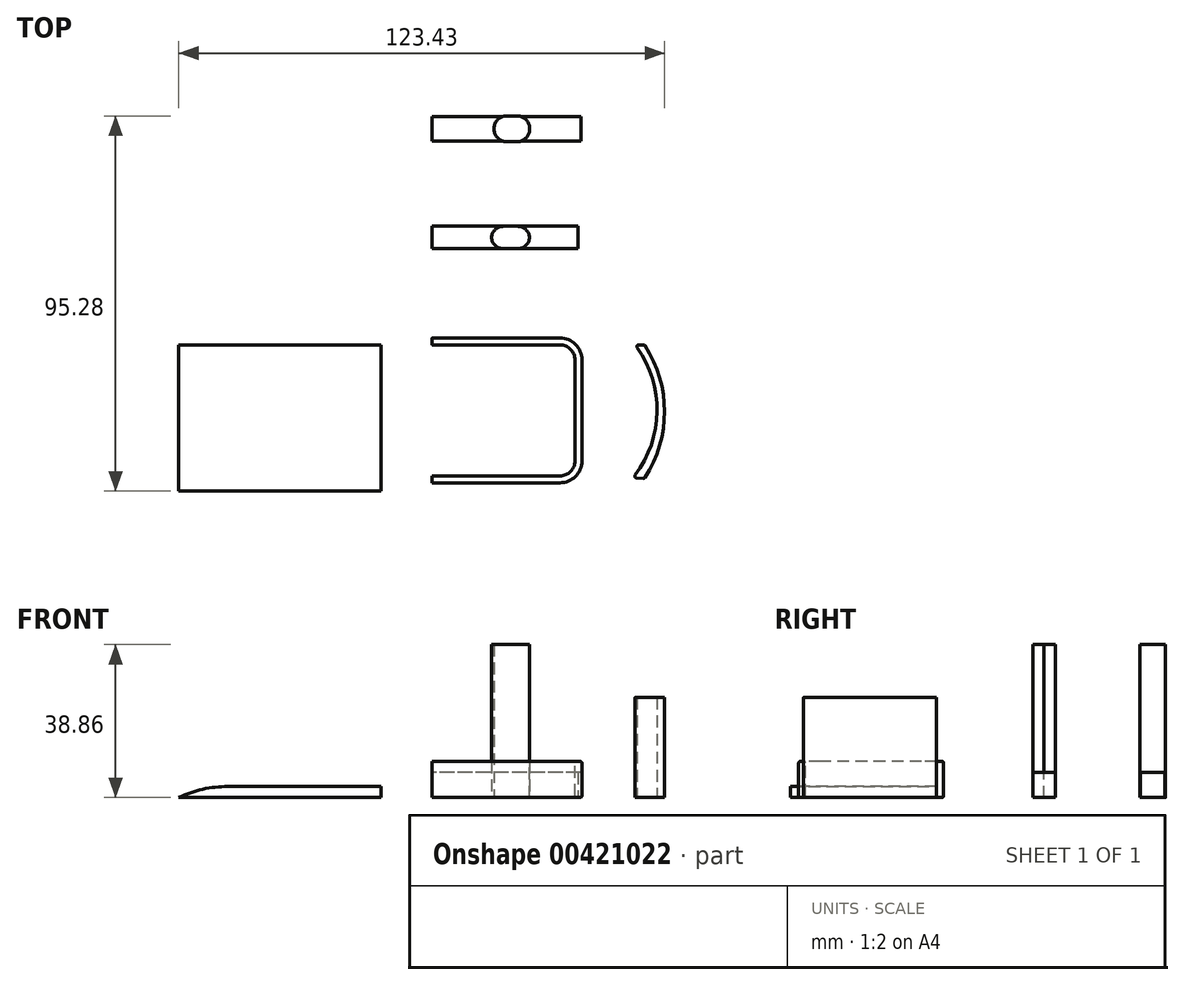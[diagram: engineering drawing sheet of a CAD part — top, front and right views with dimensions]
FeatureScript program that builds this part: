
annotation { "Feature Type Name" : "Feature", "Feature Type Description" : "" }
export const myFeature = defineFeature(function(context is Context, id is Id, definition is map)
    precondition{}
    {
        {
            var Q0;
            Q0=qCreatedBy(makeId("Top.planeOp"),FACE);
            var sketch = newSketch(context, id + "F0", { "sketchPlane" : qUnion([Q0])});
            skLineSegment(sketch, "E0", {"start": v(0, -33.26) * mm, "end": v(32.47, -33.26) * mm});
            skLineSegment(sketch, "E1", {"start": v(36.28, -29.45) * mm, "end": v(36.28, -3.81) * mm});
            skPoint(sketch, "E2.visualSharp", {"position": v(36.28, -33.26) * mm});
            skArc(sketch, "E2.filletArc", {"start": v(32.47, -33.26) * mm, "mid": v(35.17, -32.14) * mm, "end": v(36.28, -29.45) * mm});
            skLineSegment(sketch, "E3", {"start": v(0, 0) * mm, "end": v(32.47, 0) * mm});
            skPoint(sketch, "E4.visualSharp", {"position": v(36.28, 0) * mm});
            skArc(sketch, "E4.filletArc", {"start": v(36.28, -3.81) * mm, "mid": v(35.17, -1.12) * mm, "end": v(32.47, 0) * mm});
            skSolve(sketch);
        }
        {
            var Q0;
            Q0=qCreatedBy(makeId("Right.planeOp"),FACE);
            var sketch = newSketch(context, id + "F1", { "sketchPlane" : qUnion([Q0])});
            skLineSegment(sketch, "E5", {"start": v(0, 0.43) * mm, "end": v(0, 8.73) * mm});
            skLineSegment(sketch, "E6", {"start": v(1.78, 8.73) * mm, "end": v(1.78, 0.43) * mm});
            skLineSegment(sketch, "E7", {"start": v(0.43, 0) * mm, "end": v(1.35, 0) * mm});
            skLineSegment(sketch, "E8", {"start": v(1.35, 9.16) * mm, "end": v(0.43, 9.16) * mm});
            skPoint(sketch, "E9.visualSharp", {"position": v(0, 9.16) * mm});
            skArc(sketch, "E9.filletArc", {"start": v(0.43, 9.16) * mm, "mid": v(0.13, 9.03) * mm, "end": v(0, 8.73) * mm});
            skPoint(sketch, "E10.visualSharp", {"position": v(1.78, 9.16) * mm});
            skArc(sketch, "E10.filletArc", {"start": v(1.78, 8.73) * mm, "mid": v(1.65, 9.03) * mm, "end": v(1.35, 9.16) * mm});
            skPoint(sketch, "E11.visualSharp", {"position": v(1.78, 0) * mm});
            skArc(sketch, "E11.filletArc", {"start": v(1.35, 0) * mm, "mid": v(1.65, 0.13) * mm, "end": v(1.78, 0.43) * mm});
            skPoint(sketch, "E12.visualSharp", {"position": v(0, 0) * mm});
            skArc(sketch, "E12.filletArc", {"start": v(0, 0.43) * mm, "mid": v(0.13, 0.13) * mm, "end": v(0.43, 0) * mm});
            skSolve(sketch);
        }
        {
            var Q0;
            Q0=makeQuery(id+"F1.imprint","IMPRINT",FACE,{"disambiguationData":[TD([[makeQuery(id+"F1.imprint","IMPRINT",EDGE,{"derivedFrom":sQuery(id+"F1.wireOp",EDGE,"E5")}),-1.0]])]});
            var Q1;
            Q1=sQuery(id+"F0.wireOp",EDGE,"E3");
            var Q2;
            Q2=sQuery(id+"F0.wireOp",EDGE,"E4.filletArc");
            var Q3;
            Q3=sQuery(id+"F0.wireOp",EDGE,"E1");
            var Q4;
            Q4=sQuery(id+"F0.wireOp",EDGE,"E2.filletArc");
            var Q5;
            Q5=sQuery(id+"F0.wireOp",EDGE,"E0");
            sweep(context, id + "F2", {"profiles" : qUnion([Q0]), "path" : qUnion([Q1, Q2, Q3, Q4, Q5])});
        }
        {
            var Q0;
            Q0=qCreatedBy(makeId("Top.planeOp"),FACE);
            var sketch = newSketch(context, id + "F3", { "sketchPlane" : qUnion([Q0])});
            skArc(sketch, "E13", {"start": v(54.13, -33.66) * mm, "mid": v(59.04, -16.93) * mm, "end": v(54.13, -0.2) * mm});
            skArc(sketch, "E14", {"start": v(51.57, -33.06) * mm, "mid": v(57.14, -16.97) * mm, "end": v(52.1, -0.72) * mm});
            skLineSegment(sketch, "E15", {"start": v(53.73, -33.87) * mm, "end": v(51.91, -33.78) * mm});
            skLineSegment(sketch, "E16", {"start": v(52.47, 0) * mm, "end": v(53.74, 0) * mm});
            skPoint(sketch, "E17.visualSharp", {"position": v(51.03, -33.74) * mm});
            skArc(sketch, "E17.filletArc", {"start": v(51.57, -33.06) * mm, "mid": v(51.52, -33.52) * mm, "end": v(51.91, -33.78) * mm});
            skPoint(sketch, "E18.visualSharp", {"position": v(54, -33.88) * mm});
            skArc(sketch, "E18.filletArc", {"start": v(53.73, -33.87) * mm, "mid": v(53.96, -33.82) * mm, "end": v(54.13, -33.66) * mm});
            skPoint(sketch, "E19.visualSharp", {"position": v(51.57, 0) * mm});
            skArc(sketch, "E19.filletArc", {"start": v(52.47, 0) * mm, "mid": v(52.06, -0.25) * mm, "end": v(52.1, -0.72) * mm});
            skPoint(sketch, "E20.visualSharp", {"position": v(54, 0) * mm});
            skArc(sketch, "E20.filletArc", {"start": v(54.13, -0.2) * mm, "mid": v(53.96, -0.06) * mm, "end": v(53.74, 0) * mm});
            skSolve(sketch);
        }
        {
            var Q0;
            Q0=qCreatedBy(makeId("Top.planeOp"),FACE);
            var sketch = newSketch(context, id + "F4", { "sketchPlane" : qUnion([Q0])});
            skSolve(sketch);
        }
        {
            var Q0;
            Q0=makeQuery(id+"F3.imprint","IMPRINT",FACE,{"disambiguationData":[TD([[makeQuery(id+"F3.imprint","IMPRINT",EDGE,{"derivedFrom":sQuery(id+"F3.wireOp",EDGE,"E13")}),1.0]])]});
            var Q1;
            Q1 = qSketchRegion(id + "F4", true);
            extrude(context, id + "F5", {"entities" : qUnion([Q0, Q1]), "depth" : 25.4 * mm});
        }
        {
            var Q0;
            Q0=qCreatedBy(makeId("Top.planeOp"),FACE);
            var sketch = newSketch(context, id + "F6", { "sketchPlane" : qUnion([Q0])});
            skLineSegment(sketch, "E21.bottom", {"start": v(-64.4, 0) * mm, "end": v(-13.02, 0) * mm});
            skLineSegment(sketch, "E21.top", {"start": v(-64.4, -37.12) * mm, "end": v(-13.02, -37.12) * mm});
            skLineSegment(sketch, "E21.left", {"start": v(-64.4, 0) * mm, "end": v(-64.4, -37.12) * mm});
            skLineSegment(sketch, "E21.right", {"start": v(-13.02, 0) * mm, "end": v(-13.02, -37.12) * mm});
            skSolve(sketch);
        }
        {
            var Q0;
            Q0 = qSketchRegion(id + "F6", true);
            var Q1;
            Q1=makeQuery(id+"F6.imprint","IMPRINT",FACE,{"disambiguationData":[TD([[makeQuery(id+"F6.imprint","IMPRINT",EDGE,{"derivedFrom":sQuery(id+"F6.wireOp",EDGE,"E21.bottom")}),-1.0]])]});
            extrude(context, id + "F7", {"entities" : qUnion([Q0, Q1]), "depth" : 2.8 * mm});
        }
        {
            var Q0;
            Q0=makeQuery(id+"F7.opExtrude","CAP_EDGE",EDGE,{"disambiguationData":[OSD([sQuery(id+"F6.wireOp",EDGE,"E21.left")])],"isStart":false});
            fillet(context, id + "F8", {"entities" : qUnion([Q0]), "radius" : 29.43 * mm, "tangentPropagation" : true, "allowEdgeOverflow" : false});
        }
        {
            var Q0;
            Q0=qCreatedBy(makeId("Top.planeOp"),FACE);
            var sketch = newSketch(context, id + "F9", { "sketchPlane" : qUnion([Q0])});
            skLineSegment(sketch, "E22.bottom", {"start": v(37.86, 58.02) * mm, "end": v(0, 58.02) * mm});
            skLineSegment(sketch, "E22.top", {"start": v(37.86, 51.75) * mm, "end": v(0, 51.75) * mm});
            skLineSegment(sketch, "E22.left", {"start": v(37.86, 58.02) * mm, "end": v(37.86, 51.75) * mm});
            skLineSegment(sketch, "E22.right", {"start": v(0, 58.02) * mm, "end": v(0, 51.75) * mm});
            skLineSegment(sketch, "E23.bottom", {"start": v(37.04, 30.23) * mm, "end": v(0, 30.23) * mm});
            skLineSegment(sketch, "E23.top", {"start": v(37.04, 24.51) * mm, "end": v(0, 24.51) * mm});
            skLineSegment(sketch, "E23.left", {"start": v(37.04, 30.23) * mm, "end": v(37.04, 24.51) * mm});
            skLineSegment(sketch, "E23.right", {"start": v(0, 30.23) * mm, "end": v(0, 24.51) * mm});
            skSolve(sketch);
        }
        {
            var Q0;
            Q0=makeQuery(id+"F9.imprint","IMPRINT",FACE,{"disambiguationData":[TD([[makeQuery(id+"F9.imprint","IMPRINT",EDGE,{"derivedFrom":sQuery(id+"F9.wireOp",EDGE,"E22.bottom")}),1.0]])]});
            var Q1;
            Q1=makeQuery(id+"F9.imprint","IMPRINT",FACE,{"disambiguationData":[TD([[makeQuery(id+"F9.imprint","IMPRINT",EDGE,{"derivedFrom":sQuery(id+"F9.wireOp",EDGE,"E23.bottom")}),1.0]])]});
            extrude(context, id + "F10", {"entities" : qUnion([Q0, Q1]), "depth" : 6.35 * mm});
        }
        {
            var Q0;
            Q0=qCreatedBy(makeId("Top.planeOp"),FACE);
            var sketch = newSketch(context, id + "F11", { "sketchPlane" : qUnion([Q0])});
            skLineSegment(sketch, "E24.bottom", {"start": v(15.75, 58.16) * mm, "end": v(24.75, 58.16) * mm});
            skLineSegment(sketch, "E24.top", {"start": v(15.75, 51.67) * mm, "end": v(24.75, 51.67) * mm});
            skLineSegment(sketch, "E24.left", {"start": v(15.75, 58.16) * mm, "end": v(15.75, 51.67) * mm});
            skLineSegment(sketch, "E24.right", {"start": v(24.75, 58.16) * mm, "end": v(24.75, 51.67) * mm});
            skLineSegment(sketch, "E25.bottom", {"start": v(15.07, 30.15) * mm, "end": v(24.75, 30.15) * mm});
            skLineSegment(sketch, "E25.top", {"start": v(15.07, 24.45) * mm, "end": v(24.75, 24.45) * mm});
            skLineSegment(sketch, "E25.left", {"start": v(15.07, 30.15) * mm, "end": v(15.07, 24.45) * mm});
            skLineSegment(sketch, "E25.right", {"start": v(24.75, 30.15) * mm, "end": v(24.75, 24.45) * mm});
            skSolve(sketch);
        }
        {
            var Q0;
            Q0 = qSketchRegion(id + "F11", true);
            extrude(context, id + "F12", {"entities" : qUnion([Q0]), "depth" : 38.86 * mm});
        }
        {
            var Q0;
            Q0=makeQuery(id+"F12.opExtrude","SWEPT_EDGE",EDGE,{"disambiguationData":[OSD([sQuery(id+"F11.wireOp",EDGE,"E25.top"),sQuery(id+"F11.wireOp",EDGE,"E25.left")])]});
            var Q1;
            Q1=makeQuery(id+"F12.opExtrude","SWEPT_EDGE",EDGE,{"disambiguationData":[OSD([sQuery(id+"F11.wireOp",EDGE,"E25.top"),sQuery(id+"F11.wireOp",EDGE,"E25.right")])]});
            var Q2;
            Q2=makeQuery(id+"F12.opExtrude","SWEPT_EDGE",EDGE,{"disambiguationData":[OSD([sQuery(id+"F11.wireOp",EDGE,"E25.bottom"),sQuery(id+"F11.wireOp",EDGE,"E25.right")])]});
            var Q3;
            Q3=makeQuery(id+"F12.opExtrude","SWEPT_EDGE",EDGE,{"disambiguationData":[OSD([sQuery(id+"F11.wireOp",EDGE,"E25.bottom"),sQuery(id+"F11.wireOp",EDGE,"E25.left")])]});
            var Q4;
            Q4=makeQuery(id+"F12.opExtrude","SWEPT_EDGE",EDGE,{"disambiguationData":[OSD([sQuery(id+"F11.wireOp",EDGE,"E24.top"),sQuery(id+"F11.wireOp",EDGE,"E24.right")])]});
            var Q5;
            Q5=makeQuery(id+"F12.opExtrude","SWEPT_EDGE",EDGE,{"disambiguationData":[OSD([sQuery(id+"F11.wireOp",EDGE,"E24.top"),sQuery(id+"F11.wireOp",EDGE,"E24.left")])]});
            var Q6;
            Q6=makeQuery(id+"F12.opExtrude","SWEPT_EDGE",EDGE,{"disambiguationData":[OSD([sQuery(id+"F11.wireOp",EDGE,"E24.bottom"),sQuery(id+"F11.wireOp",EDGE,"E24.right")])]});
            var Q7;
            Q7=makeQuery(id+"F12.opExtrude","SWEPT_EDGE",EDGE,{"disambiguationData":[OSD([sQuery(id+"F11.wireOp",EDGE,"E24.bottom"),sQuery(id+"F11.wireOp",EDGE,"E24.left")])]});
            fillet(context, id + "F13", {"entities" : qUnion([Q0, Q1, Q2, Q3, Q4, Q5, Q6, Q7]), "radius" : 3.07 * mm, "tangentPropagation" : true, "allowEdgeOverflow" : false});
        }
    });
